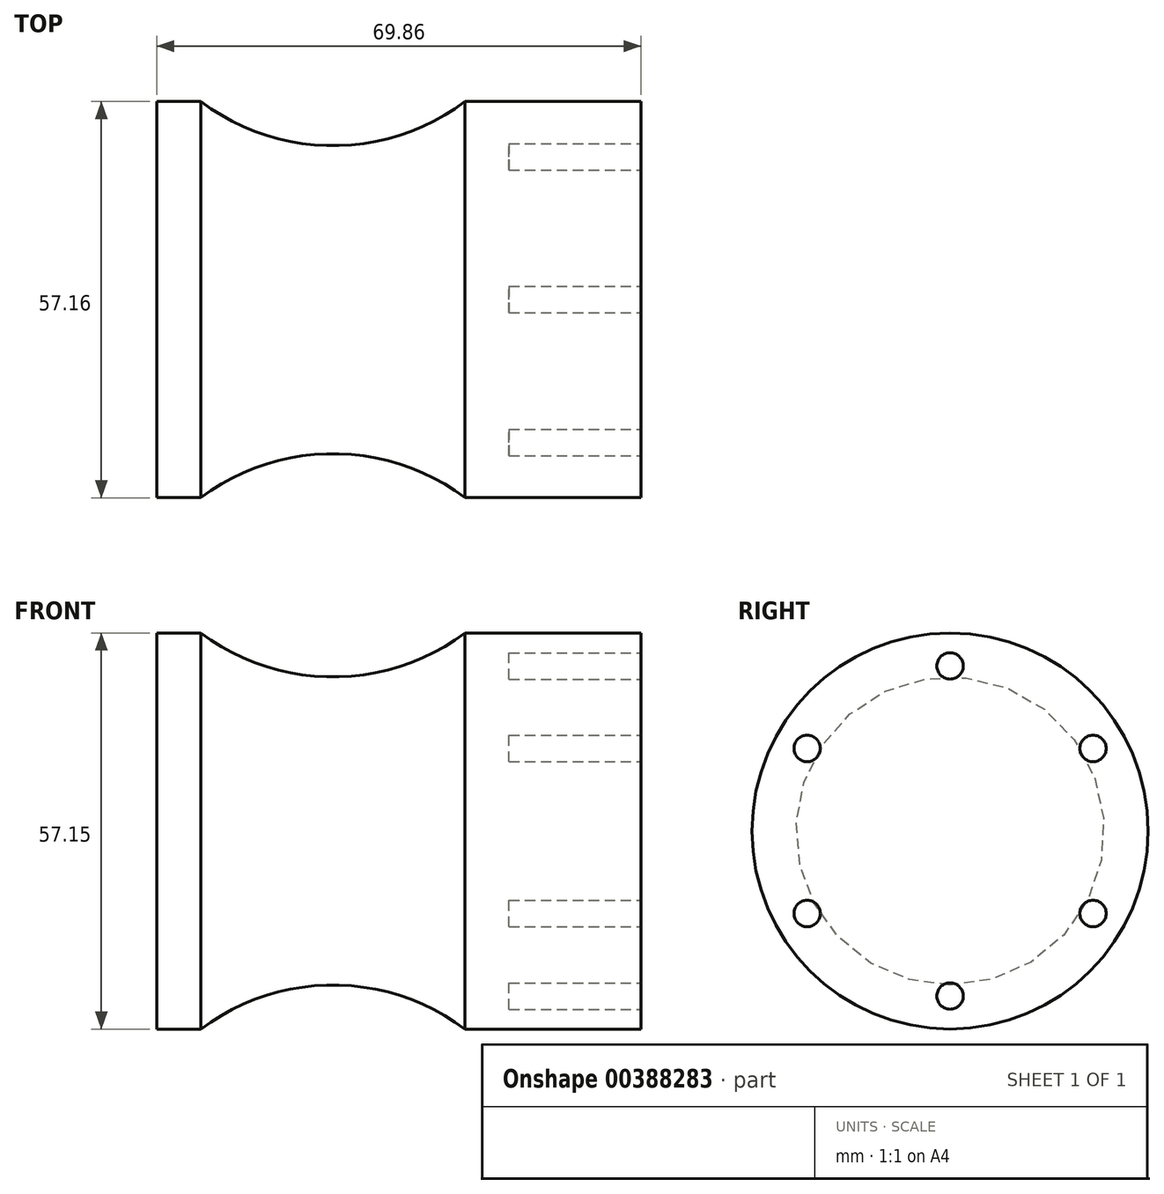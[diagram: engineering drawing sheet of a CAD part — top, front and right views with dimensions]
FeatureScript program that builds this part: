
annotation { "Feature Type Name" : "Feature", "Feature Type Description" : "" }
export const myFeature = defineFeature(function(context is Context, id is Id, definition is map)
    precondition{}
    {
        {
            var Q0;
            Q0=qCreatedBy(makeId("Front.planeOp"),FACE);
            var sketch = newSketch(context, id + "F0", { "sketchPlane" : qUnion([Q0])});
            skPoint(sketch, "E0.middle", {"position": v(0, 0) * mm});
            skLineSegment(sketch, "E1.bottom", {"start": v(34.92, 14.29) * mm, "end": v(9.52, 14.29) * mm});
            skLineSegment(sketch, "E1.top", {"start": v(34.93, -14.29) * mm, "end": v(-34.92, -14.29) * mm});
            skLineSegment(sketch, "E1.left", {"start": v(34.92, 14.29) * mm, "end": v(34.93, -14.29) * mm});
            skLineSegment(sketch, "E1.right", {"start": v(-34.93, 14.29) * mm, "end": v(-34.92, -14.29) * mm});
            skPoint(sketch, "E2", {"position": v(-28.58, 14.29) * mm});
            skPoint(sketch, "E3", {"position": v(9.52, 14.29) * mm});
            skArc(sketch, "E4", {"start": v(-28.58, 14.29) * mm, "mid": v(-9.53, 7.94) * mm, "end": v(9.52, 14.29) * mm});
            skLineSegment(sketch, "E5.trimOffspring", {"start": v(-28.58, 14.29) * mm, "end": v(-34.93, 14.29) * mm});
            skSolve(sketch);
        }
        {
            var Q0;
            Q0=makeQuery(id+"F0.imprint","IMPRINT",FACE,{"disambiguationData":[TD([[makeQuery(id+"F0.imprint","IMPRINT",EDGE,{"derivedFrom":sQuery(id+"F0.wireOp",EDGE,"E1.bottom")}),1.0]])]});
            var Q1;
            Q1=sQuery(id+"F0.wireOp",EDGE,"E1.top");
            revolve(context, id + "F1", {"entities" : qUnion([Q0]), "axis" : qUnion([Q1]), "revolveType" : RevolveType.FULL});
        }
        {
            var Q0;
            Q0=makeQuery(id+"F1.opRevolve","SWEPT_FACE",FACE,{"disambiguationData":[OSD([sQuery(id+"F0.wireOp",EDGE,"E1.left")])]});
            var sketch = newSketch(context, id + "F2", { "sketchPlane" : qUnion([Q0])});
            skCircle(sketch, "E6", {"center": v(0, -14.29) * mm, "radius": 23.81 * mm, "construction": true});
            skCircle(sketch, "E7", {"center": v(0, 9.53) * mm, "radius": 1.9 * mm});
            skCircle(sketch, "E8.1.0", {"center": v(-20.62, -2.38) * mm, "radius": 1.9 * mm});
            skCircle(sketch, "E8.2.0", {"center": v(-20.62, -26.2) * mm, "radius": 1.9 * mm});
            skCircle(sketch, "E8.3.0", {"center": v(0, -38.1) * mm, "radius": 1.9 * mm});
            skCircle(sketch, "E8.4.0", {"center": v(20.62, -26.2) * mm, "radius": 1.9 * mm});
            skCircle(sketch, "E8.5.0", {"center": v(20.62, -2.38) * mm, "radius": 1.9 * mm});
            skSolve(sketch);
        }
        {
            var Q0;
            Q0=makeQuery(id+"F2.imprint","IMPRINT",FACE,{"disambiguationData":[TD([[makeQuery(id+"F2.imprint","IMPRINT",EDGE,{"derivedFrom":sQuery(id+"F2.wireOp",EDGE,"E7")}),1.0]])]});
            var Q1;
            Q1=makeQuery(id+"F2.imprint","IMPRINT",FACE,{"disambiguationData":[TD([[makeQuery(id+"F2.imprint","IMPRINT",EDGE,{"derivedFrom":sQuery(id+"F2.wireOp",EDGE,"E8.1.0")}),1.0]])]});
            var Q2;
            Q2=makeQuery(id+"F2.imprint","IMPRINT",FACE,{"disambiguationData":[TD([[makeQuery(id+"F2.imprint","IMPRINT",EDGE,{"derivedFrom":sQuery(id+"F2.wireOp",EDGE,"E8.2.0")}),1.0]])]});
            var Q3;
            Q3=makeQuery(id+"F2.imprint","IMPRINT",FACE,{"disambiguationData":[TD([[makeQuery(id+"F2.imprint","IMPRINT",EDGE,{"derivedFrom":sQuery(id+"F2.wireOp",EDGE,"E8.3.0")}),1.0]])]});
            var Q4;
            Q4=makeQuery(id+"F2.imprint","IMPRINT",FACE,{"disambiguationData":[TD([[makeQuery(id+"F2.imprint","IMPRINT",EDGE,{"derivedFrom":sQuery(id+"F2.wireOp",EDGE,"E8.4.0")}),1.0]])]});
            var Q5;
            Q5=makeQuery(id+"F2.imprint","IMPRINT",FACE,{"disambiguationData":[TD([[makeQuery(id+"F2.imprint","IMPRINT",EDGE,{"derivedFrom":sQuery(id+"F2.wireOp",EDGE,"E8.5.0")}),1.0]])]});
            extrude(context, id + "F3", {"entities" : qUnion([Q0, Q1, Q2, Q3, Q4, Q5]), "operationType" : NewBodyOperationType.REMOVE, "oppositeDirection" : true, "depth" : 19.05 * mm});
        }
    });
